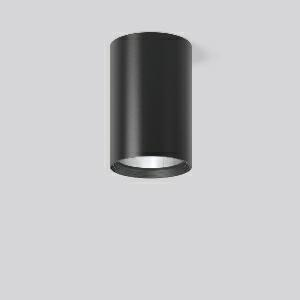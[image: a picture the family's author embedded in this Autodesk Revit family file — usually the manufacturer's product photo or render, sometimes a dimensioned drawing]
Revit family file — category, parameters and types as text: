
# Revit family: heledon_maxi_a_931246_003_2_76_b3ba
name_source: partatom
category: Lighting Fixtures
units: mm (PartAtom-declared; Revit-internal decimal feet)

## family parameters
Cut with Voids When Loaded = No
Host = Face
Light Source = No
Part Type = Normal
Room Calculation Point = No
Round Connector Dimension = Use Diameter
Shared = No

## types (1)
- HELEDON maxi A (1 x LED Modul 927 bakery, 3450 lm, 2700)
    Apparent Load = 33 VA
    Approval mark = CE
    CIE Flux Codes = 100 100 100 100 100
    Color Rendering = 90
    Color Temperature = 2700
    Default Elevation = 1800 mm
    Description = Series: HELEDON maxi
Cylindrical surface-mounted downlight. Housing: die-cast aluminium, powder-coated. Internal ceiling frame polycarbonate with bayonet mounting. Black plastic ring and recessed LED to prevent glare from the side. Optical assembly with reflector made of MIRO-Silver with 98% total light reflection for outstanding efficiency - can be changed without tools. Special LED for illumination of pastries included. Suitable for Ceiling mounting. Easy installation with a separate ceiling frame with bayonet mounting and plug connection. Driver integrated. Connected via plug-in connector. High quality converter without flickering and stroboscopic effect. The following accessories can be mounted without use of tools: interchangeable lenses, decorative glasses, honeycomb louvre, clear and frosted diffusers, white interchangeable plastic ring. 
Colour: deep black, matt (RAL 9005)
Diameter: 123 mm
Height: 183 mm
Lamp: LED
Socket: without socket
Colour temperature: bakery
Colour rendering index (CRI): 97
System power: 33 W
Rated luminous flux: 3450 lm
Luminous efficiency: 105 lm/W
Control gear: Converter, dimmable, DALI
Protection class: I
Type of protection: IP 20
    Height = 183 mm
    Lamp = 1 x LED Modul 927 bakery
    Lamp Light Flux = 3450 lm
    Lamp count = 1
    Length = 123 mm
    Lifetime = 50000 h
    Luminous efficacy = 105 lm/W
    Manufacturer = RZB
    ModVariant = No
    Model = 931246.003.2.76
    Mounting Place = Ceiling
    Mounting Type = Surface mounted
    Number of Poles = 1
    OnlyDefault = Yes
    Power Factor = 1
    Product Name = HELEDON maxi A
    Product group = Surface mounted downlights
    ProductGroupID = 302
    Protection Class = Protection class I
    Protection Degree = IP 20
    RLX_Detail_Level = 1
    RLX_Emergency_Light_Flux = 0 lm
    RLX_Emergency_Type = 0
    RLX_Emergency_Type_DB = No
    RlxData = <blob elided: 97705 chars, md5=b8c264d0>
    Socket = socket
    Standby Power = 0 W
    System Light Flux = 3450 lm
    System Power = 33 W
    Type Comments = Product without accessories
    Type Image = 931192.003.jpg
    URL = http://relux.com
    VarID = ---
    Voltage = 230 V
    Voltage Range = 220-240 V
    Weight = 0.00 kg
    Width = 0 mm  [stored 0 ft]

note: [stored X ft] marks values corroborated as IEEE doubles in the binary element streams (Revit-internal decimal feet)

## geometry (parser evidence)
native form markers: Blend x4, Sweep x11
no freeform markers — native parametric forms only
